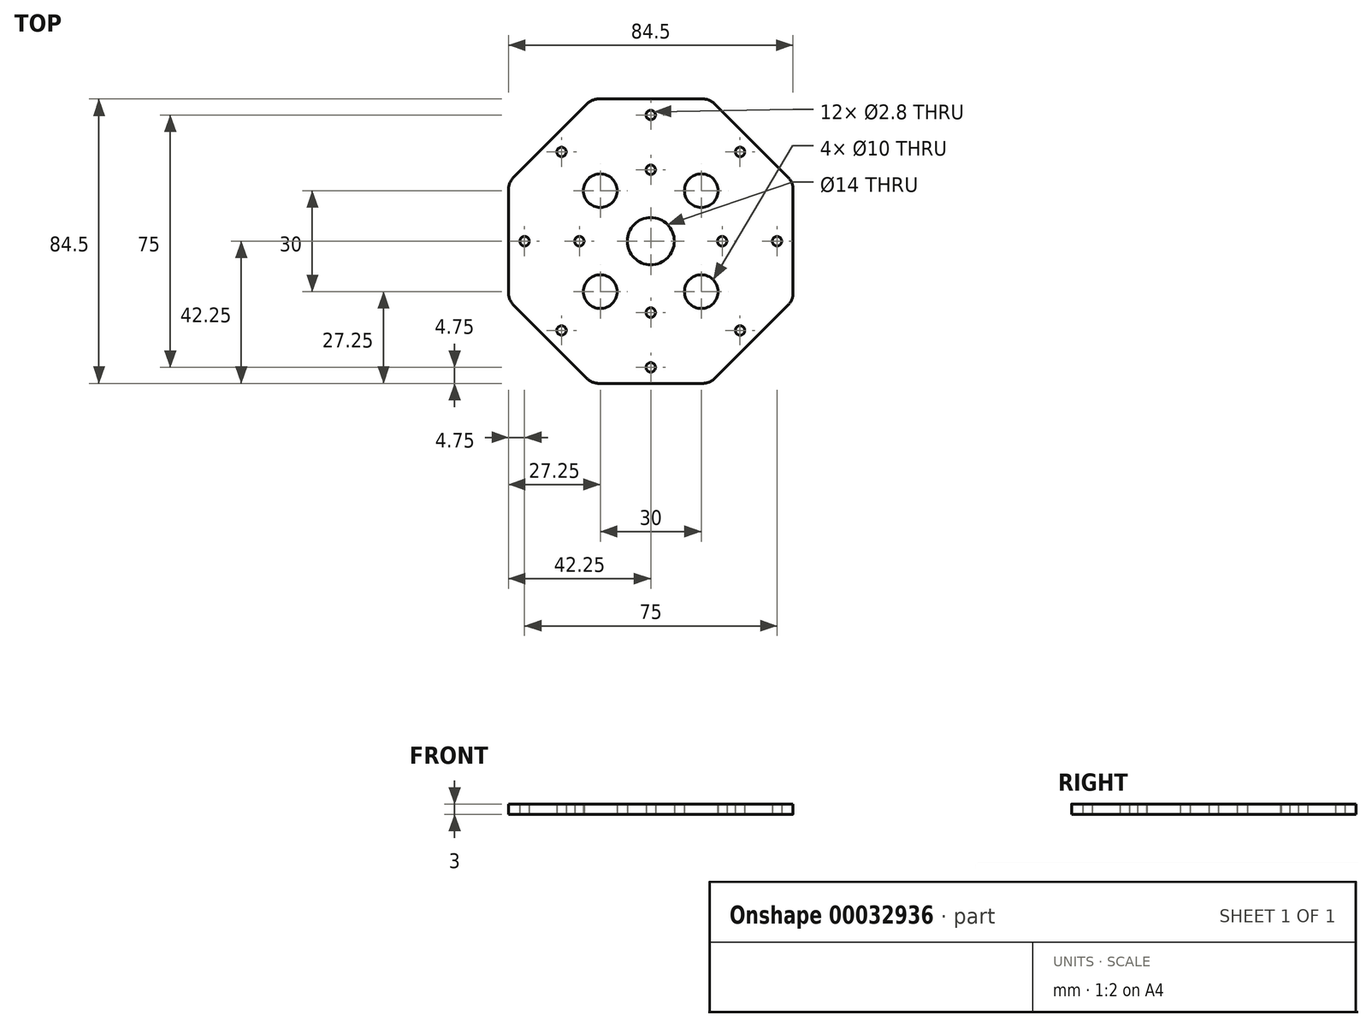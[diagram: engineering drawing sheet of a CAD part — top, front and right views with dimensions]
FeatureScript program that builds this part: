
annotation { "Feature Type Name" : "Feature", "Feature Type Description" : "" }
export const myFeature = defineFeature(function(context is Context, id is Id, definition is map)
    precondition{}
    {
        {
            var Q0;
            Q0=qCreatedBy(makeId("Top.planeOp"),FACE);
            var sketch = newSketch(context, id + "F0", { "sketchPlane" : qUnion([Q0])});
            skLineSegment(sketch, "E0.rect.bottom", {"start": v(15, -15) * mm, "end": v(-15, -15) * mm, "construction": true});
            skLineSegment(sketch, "E0.rect.top", {"start": v(15, 15) * mm, "end": v(-15, 15) * mm, "construction": true});
            skLineSegment(sketch, "E0.rect.left", {"start": v(15, -15) * mm, "end": v(15, 15) * mm, "construction": true});
            skLineSegment(sketch, "E0.rect.right", {"start": v(-15, -15) * mm, "end": v(-15, 15) * mm, "construction": true});
            skPoint(sketch, "E0.rect.middle", {"position": v(0, 0) * mm});
            skCircle(sketch, "E1.cCircle", {"center": v(0, 0) * mm, "radius": 21.21 * mm, "construction": true});
            skLineSegment(sketch, "E1.0", {"start": v(21.21, 0) * mm, "end": v(0, -21.21) * mm, "construction": true});
            skLineSegment(sketch, "E1.1", {"start": v(0, -21.21) * mm, "end": v(-21.21, 0) * mm, "construction": true});
            skLineSegment(sketch, "E1.2", {"start": v(-21.21, 0) * mm, "end": v(0, 21.21) * mm, "construction": true});
            skLineSegment(sketch, "E1.3", {"start": v(0, 21.21) * mm, "end": v(21.21, 0) * mm, "construction": true});
            skCircle(sketch, "E2", {"center": v(0, 21.21) * mm, "radius": 1.4 * mm});
            skCircle(sketch, "E3.1.0", {"center": v(-21.21, 0) * mm, "radius": 1.4 * mm});
            skCircle(sketch, "E3.2.0", {"center": v(0, -21.21) * mm, "radius": 1.4 * mm});
            skCircle(sketch, "E3.3.0", {"center": v(21.21, 0) * mm, "radius": 1.4 * mm});
            skCircle(sketch, "E4.cCircle", {"center": v(0, 0) * mm, "radius": 42.25 * mm, "construction": true});
            skLineSegment(sketch, "E4.0", {"start": v(-15.43, 42.25) * mm, "end": v(15.43, 42.25) * mm});
            skLineSegment(sketch, "E4.1", {"start": v(18.96, 40.78) * mm, "end": v(40.78, 18.96) * mm});
            skLineSegment(sketch, "E4.2", {"start": v(42.25, 15.43) * mm, "end": v(42.25, -15.43) * mm});
            skLineSegment(sketch, "E4.3", {"start": v(40.78, -18.96) * mm, "end": v(18.96, -40.78) * mm});
            skLineSegment(sketch, "E4.4", {"start": v(15.43, -42.25) * mm, "end": v(-15.43, -42.25) * mm});
            skLineSegment(sketch, "E4.5", {"start": v(-18.96, -40.78) * mm, "end": v(-40.78, -18.96) * mm});
            skLineSegment(sketch, "E4.6", {"start": v(-42.25, -15.43) * mm, "end": v(-42.25, 15.43) * mm});
            skLineSegment(sketch, "E4.7", {"start": v(-40.78, 18.96) * mm, "end": v(-18.96, 40.78) * mm});
            skPoint(sketch, "E4.0.midPoint", {"position": v(0, 42.25) * mm});
            skCircle(sketch, "E5", {"center": v(0, 0) * mm, "radius": 7 * mm});
            skCircle(sketch, "E6", {"center": v(0, 0) * mm, "radius": 37.5 * mm, "construction": true});
            skLineSegment(sketch, "E7", {"start": v(0, 0) * mm, "end": v(26.52, 26.52) * mm, "construction": true});
            skCircle(sketch, "E8", {"center": v(26.52, 26.52) * mm, "radius": 1.4 * mm});
            skCircle(sketch, "E9.1.0", {"center": v(0, 37.5) * mm, "radius": 1.4 * mm});
            skCircle(sketch, "E9.2.0", {"center": v(-26.52, 26.52) * mm, "radius": 1.4 * mm});
            skCircle(sketch, "E9.3.0", {"center": v(-37.5, 0) * mm, "radius": 1.4 * mm});
            skCircle(sketch, "E10.1.4.0", {"center": v(-26.52, -26.52) * mm, "radius": 1.4 * mm});
            skCircle(sketch, "E10.1.5.0", {"center": v(0, -37.5) * mm, "radius": 1.4 * mm});
            skCircle(sketch, "E10.1.6.0", {"center": v(26.52, -26.52) * mm, "radius": 1.4 * mm});
            skCircle(sketch, "E10.1.7.0", {"center": v(37.5, 0) * mm, "radius": 1.4 * mm});
            skCircle(sketch, "E11", {"center": v(15, 15) * mm, "radius": 5 * mm});
            skCircle(sketch, "E12.1.0", {"center": v(-15, 15) * mm, "radius": 5 * mm});
            skCircle(sketch, "E12.2.0", {"center": v(-15, -15) * mm, "radius": 5 * mm});
            skCircle(sketch, "E12.3.0", {"center": v(15, -15) * mm, "radius": 5 * mm});
            skPoint(sketch, "E13.visualSharp", {"position": v(-17.5, 42.25) * mm});
            skArc(sketch, "E13.filletArc", {"start": v(-15.43, 42.25) * mm, "mid": v(-17.34, 41.87) * mm, "end": v(-18.96, 40.78) * mm});
            skPoint(sketch, "E14.visualSharp", {"position": v(-42.25, 17.5) * mm});
            skArc(sketch, "E14.filletArc", {"start": v(-40.78, 18.96) * mm, "mid": v(-41.87, 17.34) * mm, "end": v(-42.25, 15.43) * mm});
            skPoint(sketch, "E15.visualSharp", {"position": v(-42.25, -17.5) * mm});
            skArc(sketch, "E15.filletArc", {"start": v(-42.25, -15.43) * mm, "mid": v(-41.87, -17.34) * mm, "end": v(-40.78, -18.96) * mm});
            skPoint(sketch, "E16.visualSharp", {"position": v(17.5, 42.25) * mm});
            skArc(sketch, "E16.filletArc", {"start": v(18.96, 40.78) * mm, "mid": v(17.34, 41.87) * mm, "end": v(15.43, 42.25) * mm});
            skPoint(sketch, "E17.visualSharp", {"position": v(42.25, 17.5) * mm});
            skArc(sketch, "E17.filletArc", {"start": v(42.25, 15.43) * mm, "mid": v(41.87, 17.34) * mm, "end": v(40.78, 18.96) * mm});
            skPoint(sketch, "E18.visualSharp", {"position": v(42.25, -17.5) * mm});
            skArc(sketch, "E18.filletArc", {"start": v(40.78, -18.96) * mm, "mid": v(41.87, -17.34) * mm, "end": v(42.25, -15.43) * mm});
            skPoint(sketch, "E19.visualSharp", {"position": v(17.5, -42.25) * mm});
            skArc(sketch, "E19.filletArc", {"start": v(15.43, -42.25) * mm, "mid": v(17.34, -41.87) * mm, "end": v(18.96, -40.78) * mm});
            skPoint(sketch, "E20.visualSharp", {"position": v(-17.5, -42.25) * mm});
            skArc(sketch, "E20.filletArc", {"start": v(-18.96, -40.78) * mm, "mid": v(-17.34, -41.87) * mm, "end": v(-15.43, -42.25) * mm});
            skSolve(sketch);
        }
        {
            var Q0;
            Q0=makeQuery(id+"F0.imprint","IMPRINT",FACE,{"disambiguationData":[TD([[makeQuery(id+"F0.imprint","IMPRINT",EDGE,{"derivedFrom":sQuery(id+"F0.wireOp",EDGE,"E2")}),-1.0]])]});
            extrude(context, id + "F1", {"entities" : qUnion([Q0]), "depth" : 3 * mm});
        }
    });
